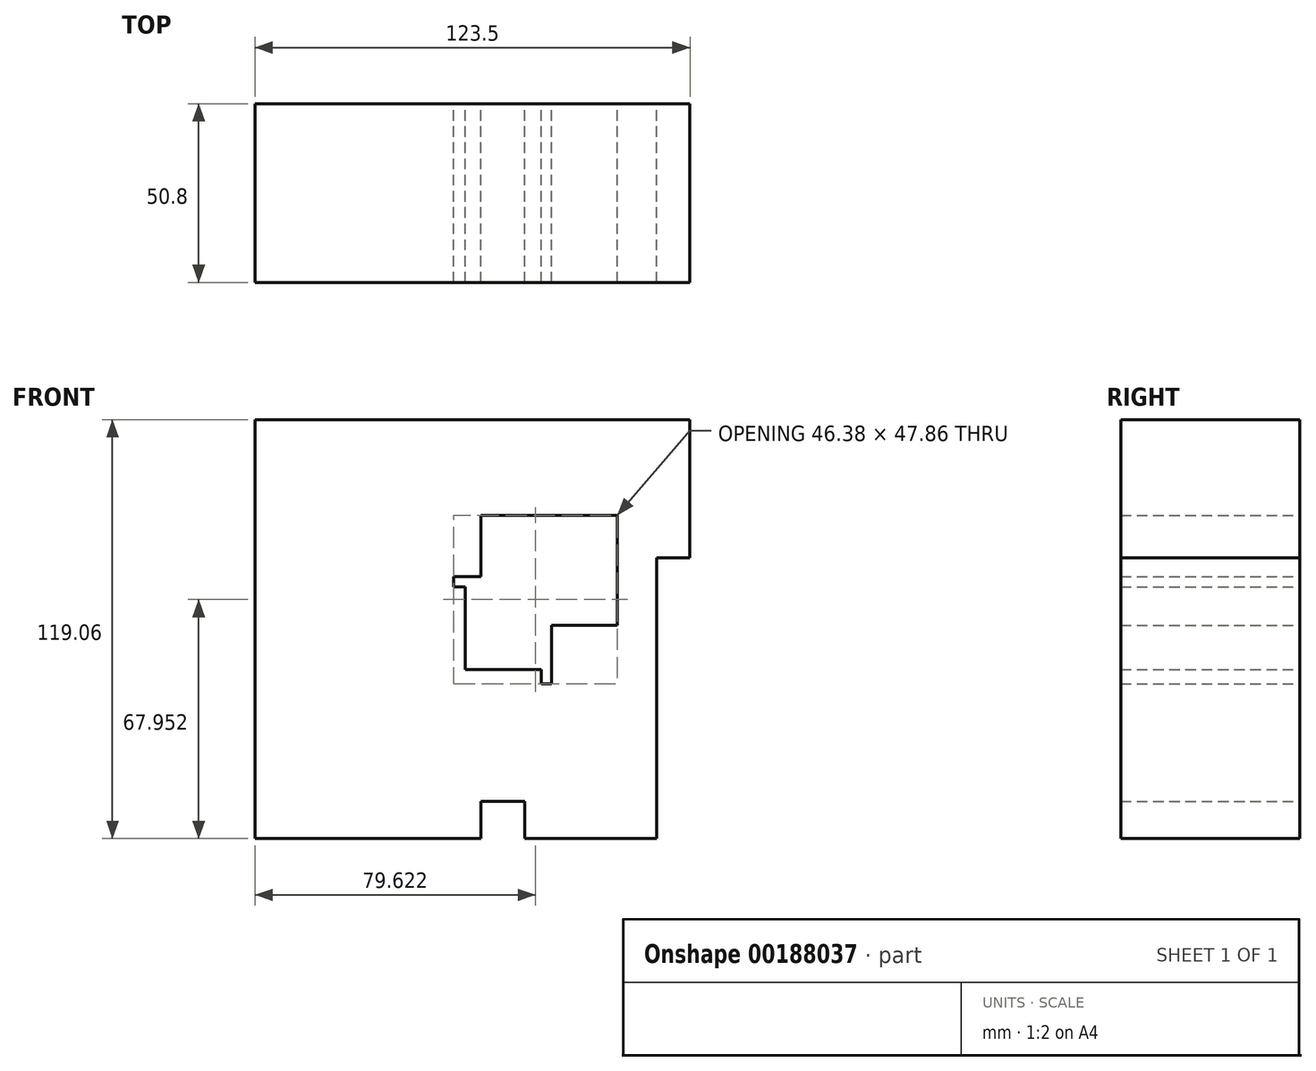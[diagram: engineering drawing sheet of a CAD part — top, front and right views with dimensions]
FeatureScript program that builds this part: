
annotation { "Feature Type Name" : "Feature", "Feature Type Description" : "" }
export const myFeature = defineFeature(function(context is Context, id is Id, definition is map)
    precondition{}
    {
        {
            var Q0;
            Q0=qCreatedBy(makeId("Front.planeOp"),FACE);
            var sketch = newSketch(context, id + "F0", { "sketchPlane" : qUnion([Q0])});
            skLineSegment(sketch, "E0.bottom", {"start": v(0, 0) * mm, "end": v(27.77, 0) * mm});
            skLineSegment(sketch, "E0.top", {"start": v(0, 43.87) * mm, "end": v(27.77, 43.87) * mm});
            skLineSegment(sketch, "E0.left", {"start": v(0, 0) * mm, "end": v(0, 43.87) * mm});
            skLineSegment(sketch, "E0.right", {"start": v(27.77, 0) * mm, "end": v(27.77, 43.87) * mm});
            skLineSegment(sketch, "E1.bottom", {"start": v(27.77, 43.87) * mm, "end": v(46.38, 43.87) * mm});
            skLineSegment(sketch, "E1.top", {"start": v(27.77, 12.56) * mm, "end": v(46.38, 12.56) * mm});
            skLineSegment(sketch, "E1.left", {"start": v(27.77, 43.87) * mm, "end": v(27.77, 12.56) * mm});
            skLineSegment(sketch, "E1.right", {"start": v(46.38, 43.87) * mm, "end": v(46.38, 12.56) * mm});
            skLineSegment(sketch, "E2.bottom", {"start": v(57.61, 16.7) * mm, "end": v(46.38, 16.7) * mm});
            skLineSegment(sketch, "E2.top", {"start": v(57.61, 31.76) * mm, "end": v(46.38, 31.76) * mm});
            skLineSegment(sketch, "E2.left", {"start": v(57.61, 16.7) * mm, "end": v(57.61, 31.76) * mm});
            skLineSegment(sketch, "E2.right", {"start": v(46.38, 16.7) * mm, "end": v(46.38, 31.76) * mm});
            skLineSegment(sketch, "E3.bottom", {"start": v(57.61, 31.76) * mm, "end": v(67.07, 31.76) * mm});
            skLineSegment(sketch, "E3.top", {"start": v(57.61, 71.05) * mm, "end": v(67.07, 71.05) * mm});
            skLineSegment(sketch, "E3.left", {"start": v(57.61, 31.76) * mm, "end": v(57.61, 71.05) * mm});
            skLineSegment(sketch, "E3.right", {"start": v(67.07, 31.76) * mm, "end": v(67.07, 71.05) * mm});
            skLineSegment(sketch, "E4.bottom", {"start": v(57.61, 71.05) * mm, "end": v(-56.43, 71.05) * mm});
            skLineSegment(sketch, "E4.top", {"start": v(57.61, -48) * mm, "end": v(-56.43, -48) * mm});
            skLineSegment(sketch, "E4.left", {"start": v(57.61, 71.05) * mm, "end": v(57.61, -48) * mm});
            skLineSegment(sketch, "E4.right", {"start": v(-56.43, 71.05) * mm, "end": v(-56.43, -48) * mm});
            skLineSegment(sketch, "E5.bottom", {"start": v(-56.43, 26.44) * mm, "end": v(7.68, 26.44) * mm});
            skLineSegment(sketch, "E5.top", {"start": v(-56.43, 61.6) * mm, "end": v(7.68, 61.6) * mm});
            skLineSegment(sketch, "E5.left", {"start": v(-56.43, 26.44) * mm, "end": v(-56.43, 61.6) * mm});
            skLineSegment(sketch, "E5.right", {"start": v(7.68, 26.44) * mm, "end": v(7.68, 61.6) * mm});
            skLineSegment(sketch, "E6.bottom", {"start": v(-20.1, 26.44) * mm, "end": v(-36.34, 26.44) * mm});
            skLineSegment(sketch, "E6.top", {"start": v(-20.1, -22.6) * mm, "end": v(-36.34, -22.6) * mm});
            skLineSegment(sketch, "E6.left", {"start": v(-20.1, 26.44) * mm, "end": v(-20.1, -22.6) * mm});
            skLineSegment(sketch, "E6.right", {"start": v(-36.34, 26.44) * mm, "end": v(-36.34, -22.6) * mm});
            skLineSegment(sketch, "E7.bottom", {"start": v(14.77, -26.15) * mm, "end": v(39.3, -26.15) * mm});
            skLineSegment(sketch, "E7.top", {"start": v(14.77, -8.72) * mm, "end": v(39.3, -8.72) * mm});
            skLineSegment(sketch, "E7.left", {"start": v(14.77, -26.15) * mm, "end": v(14.77, -8.72) * mm});
            skLineSegment(sketch, "E7.right", {"start": v(39.3, -26.15) * mm, "end": v(39.3, -8.72) * mm});
            skLineSegment(sketch, "E8.bottom", {"start": v(7.68, -12.56) * mm, "end": v(-9.16, -12.56) * mm});
            skLineSegment(sketch, "E8.top", {"start": v(7.68, -22.6) * mm, "end": v(-9.16, -22.6) * mm});
            skLineSegment(sketch, "E8.left", {"start": v(7.68, -12.56) * mm, "end": v(7.68, -22.6) * mm});
            skLineSegment(sketch, "E8.right", {"start": v(-9.16, -12.56) * mm, "end": v(-9.16, -22.6) * mm});
            skLineSegment(sketch, "E9.bottom", {"start": v(-6.2, 0) * mm, "end": v(3.25, 0) * mm});
            skLineSegment(sketch, "E9.top", {"start": v(-6.2, 23.49) * mm, "end": v(3.25, 23.49) * mm});
            skLineSegment(sketch, "E9.left", {"start": v(-6.2, 0) * mm, "end": v(-6.2, 23.49) * mm});
            skLineSegment(sketch, "E9.right", {"start": v(3.25, 0) * mm, "end": v(3.25, 23.49) * mm});
            skLineSegment(sketch, "E10.bottom", {"start": v(12.7, 19.94) * mm, "end": v(12.7, 19.94) * mm});
            skLineSegment(sketch, "E10.top", {"start": v(12.7, 12.56) * mm, "end": v(12.7, 12.56) * mm});
            skLineSegment(sketch, "E10.left", {"start": v(12.7, 19.94) * mm, "end": v(12.7, 12.56) * mm});
            skLineSegment(sketch, "E10.right", {"start": v(12.7, 19.94) * mm, "end": v(12.7, 12.56) * mm});
            skLineSegment(sketch, "E11.bottom", {"start": v(9.16, -6.65) * mm, "end": v(31.32, -6.65) * mm});
            skLineSegment(sketch, "E11.top", {"start": v(9.16, 8.12) * mm, "end": v(31.32, 8.12) * mm});
            skLineSegment(sketch, "E11.left", {"start": v(9.16, -6.65) * mm, "end": v(9.16, 8.12) * mm});
            skLineSegment(sketch, "E11.right", {"start": v(31.32, -6.65) * mm, "end": v(31.32, 8.12) * mm});
            skLineSegment(sketch, "E12.bottom", {"start": v(27.77, 0) * mm, "end": v(24.82, 0) * mm});
            skLineSegment(sketch, "E12.top", {"start": v(27.77, -3.99) * mm, "end": v(24.82, -3.99) * mm});
            skLineSegment(sketch, "E12.left", {"start": v(27.77, 0) * mm, "end": v(27.77, -3.99) * mm});
            skLineSegment(sketch, "E12.right", {"start": v(24.82, 0) * mm, "end": v(24.82, -3.99) * mm});
            skLineSegment(sketch, "E13.bottom", {"start": v(17.14, -25.56) * mm, "end": v(14.77, -25.56) * mm});
            skLineSegment(sketch, "E13.top", {"start": v(17.14, -26.15) * mm, "end": v(14.77, -26.15) * mm});
            skLineSegment(sketch, "E13.left", {"start": v(17.14, -25.56) * mm, "end": v(17.14, -26.15) * mm});
            skLineSegment(sketch, "E13.right", {"start": v(14.77, -25.56) * mm, "end": v(14.77, -26.15) * mm});
            skLineSegment(sketch, "E14.bottom", {"start": v(13.89, -27.92) * mm, "end": v(-3.55, -27.92) * mm});
            skLineSegment(sketch, "E14.top", {"start": v(13.89, -14.62) * mm, "end": v(-3.55, -14.62) * mm});
            skLineSegment(sketch, "E14.left", {"start": v(13.89, -27.92) * mm, "end": v(13.89, -14.62) * mm});
            skLineSegment(sketch, "E14.right", {"start": v(-3.55, -27.92) * mm, "end": v(-3.55, -14.62) * mm});
            skLineSegment(sketch, "E15.bottom", {"start": v(-19.8, 6.35) * mm, "end": v(-26.89, 6.35) * mm});
            skLineSegment(sketch, "E15.top", {"start": v(-19.8, 54.5) * mm, "end": v(-26.89, 54.5) * mm});
            skLineSegment(sketch, "E15.left", {"start": v(-19.8, 6.35) * mm, "end": v(-19.8, 54.5) * mm});
            skLineSegment(sketch, "E15.right", {"start": v(-26.89, 6.35) * mm, "end": v(-26.89, 54.5) * mm});
            skLineSegment(sketch, "E16.bottom", {"start": v(-26.89, 54.5) * mm, "end": v(39.3, 54.5) * mm});
            skLineSegment(sketch, "E16.top", {"start": v(-26.89, -26.15) * mm, "end": v(39.3, -26.15) * mm});
            skLineSegment(sketch, "E16.left", {"start": v(-26.89, 54.5) * mm, "end": v(-26.89, -26.15) * mm});
            skLineSegment(sketch, "E16.right", {"start": v(39.3, 54.5) * mm, "end": v(39.3, -26.15) * mm});
            skLineSegment(sketch, "E17.bottom", {"start": v(36.93, -24.67) * mm, "end": v(39.3, -24.67) * mm});
            skLineSegment(sketch, "E17.top", {"start": v(36.93, -43.58) * mm, "end": v(39.3, -43.58) * mm});
            skLineSegment(sketch, "E17.left", {"start": v(36.93, -24.67) * mm, "end": v(36.93, -43.58) * mm});
            skLineSegment(sketch, "E17.right", {"start": v(39.3, -24.67) * mm, "end": v(39.3, -43.58) * mm});
            skLineSegment(sketch, "E18.bottom", {"start": v(20.1, -48) * mm, "end": v(7.68, -48) * mm});
            skLineSegment(sketch, "E18.top", {"start": v(20.1, -37.37) * mm, "end": v(7.68, -37.37) * mm});
            skLineSegment(sketch, "E18.left", {"start": v(20.1, -48) * mm, "end": v(20.1, -37.37) * mm});
            skLineSegment(sketch, "E18.right", {"start": v(7.68, -48) * mm, "end": v(7.68, -37.37) * mm});
            skSolve(sketch);
        }
        {
            var Q0;
            {var subQ31=sQuery(id+"F0.wireOp",EDGE,"E2.bottom");Q0=makeQuery(id+"F0.imprint","IMPRINT",FACE,{"disambiguationData":[TD([[makeQuery(id+"F0.imprint","IMPRINT",EDGE,{"derivedFrom":subQ31}),1.0]])]});}
            var Q1;
            {var subQ0=sQuery(id+"F0.wireOp",EDGE,"E2.bottom");Q1=makeQuery(id+"F0.imprint","IMPRINT",FACE,{"disambiguationData":[TD([[makeQuery(id+"F0.imprint","IMPRINT",EDGE,{"derivedFrom":subQ0}),-1.0]])]});}
            var Q2;
            {var subQ5=sQuery(id+"F0.wireOp",EDGE,"E9.right");Q2=makeQuery(id+"F0.imprint","IMPRINT",FACE,{"disambiguationData":[TD([[makeQuery(id+"F0.imprint","IMPRINT",EDGE,{"derivedFrom":subQ5}),1.0]])]});}
            var Q3;
            {var subQ42=sQuery(id+"F0.wireOp",EDGE,"E7.top");Q3=makeQuery(id+"F0.imprint","IMPRINT",FACE,{"disambiguationData":[TD([[makeQuery(id+"F0.imprint","IMPRINT",EDGE,{"derivedFrom":subQ42}),1.0]])]});}
            var Q4;
            {var subQ1=sQuery(id+"F0.wireOp",EDGE,"E8.bottom");Q4=makeQuery(id+"F0.imprint","IMPRINT",FACE,{"disambiguationData":[TD([[makeQuery(id+"F0.imprint","IMPRINT",EDGE,{"derivedFrom":subQ1}),1.0]])]});}
            var Q5;
            {var subQ0=sQuery(id+"F0.wireOp",EDGE,"E8.left");var subQ1=sQuery(id+"F0.wireOp",EDGE,"E8.top");var subQ2=makeQuery(id+"F0.imprint","INTERSECT",VERTEX,{"derivedFrom":[subQ1,subQ0]});Q5=makeQuery(id+"F0.imprint","IMPRINT",FACE,{"disambiguationData":[TD([[makeQuery(id+"F0.imprint","IMPRINT",EDGE,{"disambiguationData":[TD([[subQ2,-1.0]])],"derivedFrom":subQ1}),-1.0]])]});}
            var Q6;
            {var subQ0=sQuery(id+"F0.wireOp",EDGE,"E16.bottom");var subQ1=sQuery(id+"F0.wireOp",EDGE,"E15.left");var subQ2=makeQuery(id+"F0.imprint","INTERSECT",VERTEX,{"derivedFrom":[subQ1,subQ0]});Q6=makeQuery(id+"F0.imprint","IMPRINT",FACE,{"disambiguationData":[TD([[makeQuery(id+"F0.imprint","IMPRINT",EDGE,{"disambiguationData":[TD([[subQ2,1.0]])],"derivedFrom":subQ1}),1.0]])]});}
            var Q7;
            {var subQ5=sQuery(id+"F0.wireOp",EDGE,"E9.left");Q7=makeQuery(id+"F0.imprint","IMPRINT",FACE,{"disambiguationData":[TD([[makeQuery(id+"F0.imprint","IMPRINT",EDGE,{"derivedFrom":subQ5}),-1.0]])]});}
            var Q8;
            {var subQ0=sQuery(id+"F0.wireOp",EDGE,"E0.left");var subQ1=sQuery(id+"F0.wireOp",EDGE,"E0.top");var subQ2=makeQuery(id+"F0.imprint","INTERSECT",VERTEX,{"derivedFrom":[subQ1,subQ0]});Q8=makeQuery(id+"F0.imprint","IMPRINT",FACE,{"disambiguationData":[TD([[makeQuery(id+"F0.imprint","IMPRINT",EDGE,{"disambiguationData":[TD([[subQ2,-1.0]])],"derivedFrom":subQ1}),-1.0]])]});}
            var Q9;
            {var subQ5=sQuery(id+"F0.wireOp",EDGE,"E11.bottom");Q9=makeQuery(id+"F0.imprint","IMPRINT",FACE,{"disambiguationData":[TD([[makeQuery(id+"F0.imprint","IMPRINT",EDGE,{"derivedFrom":subQ5}),1.0]])]});}
            var Q10;
            {var subQ5=sQuery(id+"F0.wireOp",EDGE,"E17.top");Q10=makeQuery(id+"F0.imprint","IMPRINT",FACE,{"disambiguationData":[TD([[makeQuery(id+"F0.imprint","IMPRINT",EDGE,{"derivedFrom":subQ5}),1.0]])]});}
            var Q11;
            {var subQ7=sQuery(id+"F0.wireOp",EDGE,"E12.bottom");Q11=makeQuery(id+"F0.imprint","IMPRINT",FACE,{"disambiguationData":[TD([[makeQuery(id+"F0.imprint","IMPRINT",EDGE,{"derivedFrom":subQ7}),-1.0]])]});}
            var Q12;
            Q12=makeQuery(id+"F0.imprint","IMPRINT",FACE,{"disambiguationData":[TD([[makeQuery(id+"F0.imprint","IMPRINT",EDGE,{"derivedFrom":sQuery(id+"F0.wireOp",EDGE,"E18.bottom")}),-1.0]])]});
            var Q13;
            {var subQ0=sQuery(id+"F0.wireOp",EDGE,"E3.bottom");Q13=makeQuery(id+"F0.imprint","IMPRINT",FACE,{"disambiguationData":[TD([[makeQuery(id+"F0.imprint","IMPRINT",EDGE,{"derivedFrom":subQ0}),1.0]])]});}
            var Q14;
            {var subQ13=sQuery(id+"F0.wireOp",EDGE,"E1.left");Q14=makeQuery(id+"F0.imprint","IMPRINT",FACE,{"disambiguationData":[TD([[makeQuery(id+"F0.imprint","IMPRINT",EDGE,{"derivedFrom":subQ13}),-1.0]])]});}
            var Q15;
            {var subQ0=sQuery(id+"F0.wireOp",EDGE,"E6.left");var subQ1=sQuery(id+"F0.wireOp",EDGE,"E6.top");var subQ2=makeQuery(id+"F0.imprint","INTERSECT",VERTEX,{"derivedFrom":[subQ1,subQ0]});Q15=makeQuery(id+"F0.imprint","IMPRINT",FACE,{"disambiguationData":[TD([[makeQuery(id+"F0.imprint","IMPRINT",EDGE,{"disambiguationData":[TD([[subQ2,-1.0]])],"derivedFrom":subQ1}),-1.0]])]});}
            var Q16;
            {var subQ0=sQuery(id+"F0.wireOp",EDGE,"E6.right");Q16=makeQuery(id+"F0.imprint","IMPRINT",FACE,{"disambiguationData":[TD([[makeQuery(id+"F0.imprint","IMPRINT",EDGE,{"derivedFrom":subQ0}),1.0]])]});}
            var Q17;
            {var subQ1=sQuery(id+"F0.wireOp",EDGE,"E5.top");Q17=makeQuery(id+"F0.imprint","IMPRINT",FACE,{"disambiguationData":[TD([[makeQuery(id+"F0.imprint","IMPRINT",EDGE,{"derivedFrom":subQ1}),-1.0]])]});}
            var Q18;
            {var subQ5=sQuery(id+"F0.wireOp",EDGE,"E8.left");var subQ6=sQuery(id+"F0.wireOp",EDGE,"E8.top");var subQ7=makeQuery(id+"F0.imprint","INTERSECT",VERTEX,{"derivedFrom":[subQ6,subQ5]});Q18=makeQuery(id+"F0.imprint","IMPRINT",FACE,{"disambiguationData":[TD([[makeQuery(id+"F0.imprint","IMPRINT",EDGE,{"disambiguationData":[TD([[subQ7,-1.0]])],"derivedFrom":subQ6}),1.0]])]});}
            var Q19;
            {var subQ3=sQuery(id+"F0.wireOp",EDGE,"E16.left");var subQ5=sQuery(id+"F0.wireOp",EDGE,"E15.bottom");var subQ7=makeQuery(id+"F0.imprint","INTERSECT",VERTEX,{"derivedFrom":[subQ5,subQ3]});Q19=makeQuery(id+"F0.imprint","IMPRINT",FACE,{"disambiguationData":[TD([[makeQuery(id+"F0.imprint","IMPRINT",EDGE,{"disambiguationData":[TD([[subQ7,1.0]])],"derivedFrom":subQ5}),-1.0]])]});}
            var Q20;
            {var subQ2=sQuery(id+"F0.wireOp",EDGE,"E7.top");Q20=makeQuery(id+"F0.imprint","IMPRINT",FACE,{"disambiguationData":[TD([[makeQuery(id+"F0.imprint","IMPRINT",EDGE,{"derivedFrom":subQ2}),-1.0]])]});}
            var Q21;
            {var subQ3=sQuery(id+"F0.wireOp",EDGE,"E2.right");Q21=makeQuery(id+"F0.imprint","IMPRINT",FACE,{"disambiguationData":[TD([[makeQuery(id+"F0.imprint","IMPRINT",EDGE,{"derivedFrom":subQ3}),1.0]])]});}
            var Q22;
            {var subQ1=sQuery(id+"F0.wireOp",EDGE,"E2.top");Q22=makeQuery(id+"F0.imprint","IMPRINT",FACE,{"disambiguationData":[TD([[makeQuery(id+"F0.imprint","IMPRINT",EDGE,{"derivedFrom":subQ1}),-1.0]])]});}
            var Q23;
            {var subQ3=sQuery(id+"F0.wireOp",EDGE,"E5.right");var subQ7=sQuery(id+"F0.wireOp",EDGE,"E0.top");var subQ8=makeQuery(id+"F0.imprint","INTERSECT",VERTEX,{"derivedFrom":[subQ7,subQ3]});Q23=makeQuery(id+"F0.imprint","IMPRINT",FACE,{"disambiguationData":[TD([[makeQuery(id+"F0.imprint","IMPRINT",EDGE,{"disambiguationData":[TD([[subQ8,-1.0]])],"derivedFrom":subQ3}),-1.0]])]});}
            var Q24;
            {var subQ0=sQuery(id+"F0.wireOp",EDGE,"E1.left");Q24=makeQuery(id+"F0.imprint","IMPRINT",FACE,{"disambiguationData":[TD([[makeQuery(id+"F0.imprint","IMPRINT",EDGE,{"derivedFrom":subQ0}),1.0]])]});}
            var Q25;
            {var subQ1=sQuery(id+"F0.wireOp",EDGE,"E0.top");var subQ5=sQuery(id+"F0.wireOp",EDGE,"E0.left");var subQ6=makeQuery(id+"F0.imprint","INTERSECT",VERTEX,{"derivedFrom":[subQ1,subQ5]});Q25=makeQuery(id+"F0.imprint","IMPRINT",FACE,{"disambiguationData":[TD([[makeQuery(id+"F0.imprint","IMPRINT",EDGE,{"disambiguationData":[TD([[subQ6,-1.0]])],"derivedFrom":subQ1}),1.0]])]});}
            var Q26;
            {var subQ0=sQuery(id+"F0.wireOp",EDGE,"E14.bottom");Q26=makeQuery(id+"F0.imprint","IMPRINT",FACE,{"disambiguationData":[TD([[makeQuery(id+"F0.imprint","IMPRINT",EDGE,{"derivedFrom":subQ0}),-1.0]])]});}
            var Q27;
            {var subQ3=sQuery(id+"F0.wireOp",EDGE,"E15.left");var subQ5=sQuery(id+"F0.wireOp",EDGE,"E15.bottom");var subQ7=makeQuery(id+"F0.imprint","INTERSECT",VERTEX,{"derivedFrom":[subQ5,subQ3]});Q27=makeQuery(id+"F0.imprint","IMPRINT",FACE,{"disambiguationData":[TD([[makeQuery(id+"F0.imprint","IMPRINT",EDGE,{"disambiguationData":[TD([[subQ7,-1.0]])],"derivedFrom":subQ5}),-1.0]])]});}
            var Q28;
            Q28=makeQuery(id+"F0.imprint","IMPRINT",FACE,{"disambiguationData":[TD([[makeQuery(id+"F0.imprint","IMPRINT",EDGE,{"derivedFrom":sQuery(id+"F0.wireOp",EDGE,"E12.bottom")}),1.0]])]});
            var Q29;
            {var subQ5=sQuery(id+"F0.wireOp",EDGE,"E17.bottom");Q29=makeQuery(id+"F0.imprint","IMPRINT",FACE,{"disambiguationData":[TD([[makeQuery(id+"F0.imprint","IMPRINT",EDGE,{"derivedFrom":subQ5}),-1.0]])]});}
            var Q30;
            Q30=makeQuery(id+"F0.imprint","IMPRINT",FACE,{"disambiguationData":[TD([[makeQuery(id+"F0.imprint","IMPRINT",EDGE,{"derivedFrom":sQuery(id+"F0.wireOp",EDGE,"E13.bottom")}),1.0]])]});
            extrude(context, id + "F1", {"entities" : qUnion([Q0, Q1, Q2, Q3, Q4, Q5, Q6, Q7, Q8, Q9, Q10, Q11, Q12, Q13, Q14, Q15, Q16, Q17, Q18, Q19, Q20, Q21, Q22, Q23, Q24, Q25, Q26, Q27, Q28, Q29, Q30]), "depth" : 25.4 * mm});
        }
        {
            var Q0;
            Q0=makeQuery(id+"F1.opExtrude","CAP_FACE",FACE,{"disambiguationData":[OSD([sQuery(id+"F0.wireOp",EDGE,"E3.bottom"),sQuery(id+"F0.wireOp",EDGE,"E3.top"),sQuery(id+"F0.wireOp",EDGE,"E3.right"),sQuery(id+"F0.wireOp",EDGE,"E4.bottom"),sQuery(id+"F0.wireOp",EDGE,"E4.top"),sQuery(id+"F0.wireOp",EDGE,"E4.left"),sQuery(id+"F0.wireOp",EDGE,"E4.right"),sQuery(id+"F0.wireOp",EDGE,"E5.left"),sQuery(id+"F0.wireOp",EDGE,"E18.bottom")])],"isStart":false});
            var sketch = newSketch(context, id + "F2", { "sketchPlane" : qUnion([Q0])});
            skFitSpline(sketch, "E19", {"points": [v(16.16, 21.39) * mm, v(7.73, 32.86) * mm, v(-10.62, 37.34) * mm, v(-25.03, 24.67) * mm, v(-29.6, 2.6) * mm, v(-27.05, -10.11) * mm, v(-21.39, -16.83) * mm, v(-17.8, -22.2) * mm, v(-15.69, -21.83) * mm, v(-14.04, -21.35) * mm, v(-6.14, -18.42) * mm, v(2.88, -11.86) * mm, v(7.17, -7.67) * mm, v(8.06, -7.23) * mm, v(9.86, -4.62) * mm, v(10.58, -3.92) * mm, v(10.95, -2.7) * mm], "startDerivative": vector(-73.06, 141.69) * mm, "endDerivative": vector(10.56, 53.2) * mm});
            skFitSpline(sketch, "E20", {"points": [v(10.95, 0) * mm, v(10.95, 2.14) * mm, v(13.3, 3.24) * mm, v(13.42, 3.64) * mm], "startDerivative": vector(-1.86, 6.17) * mm, "endDerivative": vector(-0.26, 2.4) * mm});
            skSolve(sketch);
        }
        {
            var Q0;
            Q0=makeQuery(id+"F2.imprint","IMPRINT",FACE,{"disambiguationData":[TD([[makeQuery(id+"F2.imprint","IMPRINT",EDGE,{"derivedFrom":makeQuery(id+"F1.opExtrude","CAP_EDGE",EDGE,{"disambiguationData":[OSD([sQuery(id+"F0.wireOp",EDGE,"E3.bottom")])],"isStart":false})}),1.0]])]});
            extrude(context, id + "F3", {"entities" : qUnion([Q0]), "operationType" : NewBodyOperationType.ADD, "depth" : 25.4 * mm});
        }
    });
